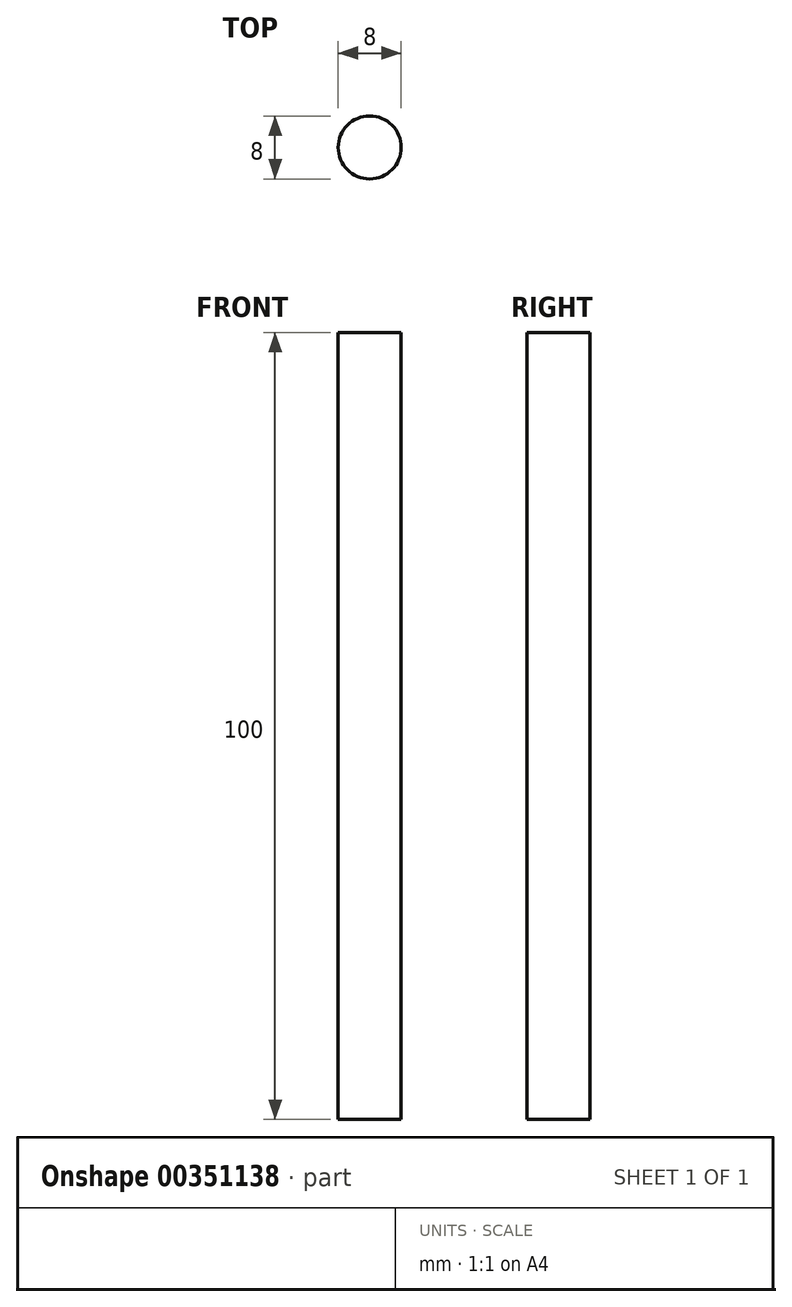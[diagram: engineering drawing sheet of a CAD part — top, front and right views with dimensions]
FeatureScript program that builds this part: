
annotation { "Feature Type Name" : "Feature", "Feature Type Description" : "" }
export const myFeature = defineFeature(function(context is Context, id is Id, definition is map)
    precondition{}
    {
        {
            var Q0;
            Q0=qCreatedBy(makeId("Top.planeOp"),FACE);
            var sketch = newSketch(context, id + "F0", { "sketchPlane" : qUnion([Q0])});
            skCircle(sketch, "E0", {"center": v(0, 0) * mm, "radius": 4 * mm});
            skSolve(sketch);
        }
        {
            var Q0;
            Q0 = qSketchRegion(id + "F0", true);
            extrude(context, id + "F1", {"entities" : qUnion([Q0]), "depth" : 100 * mm});
        }
    });
